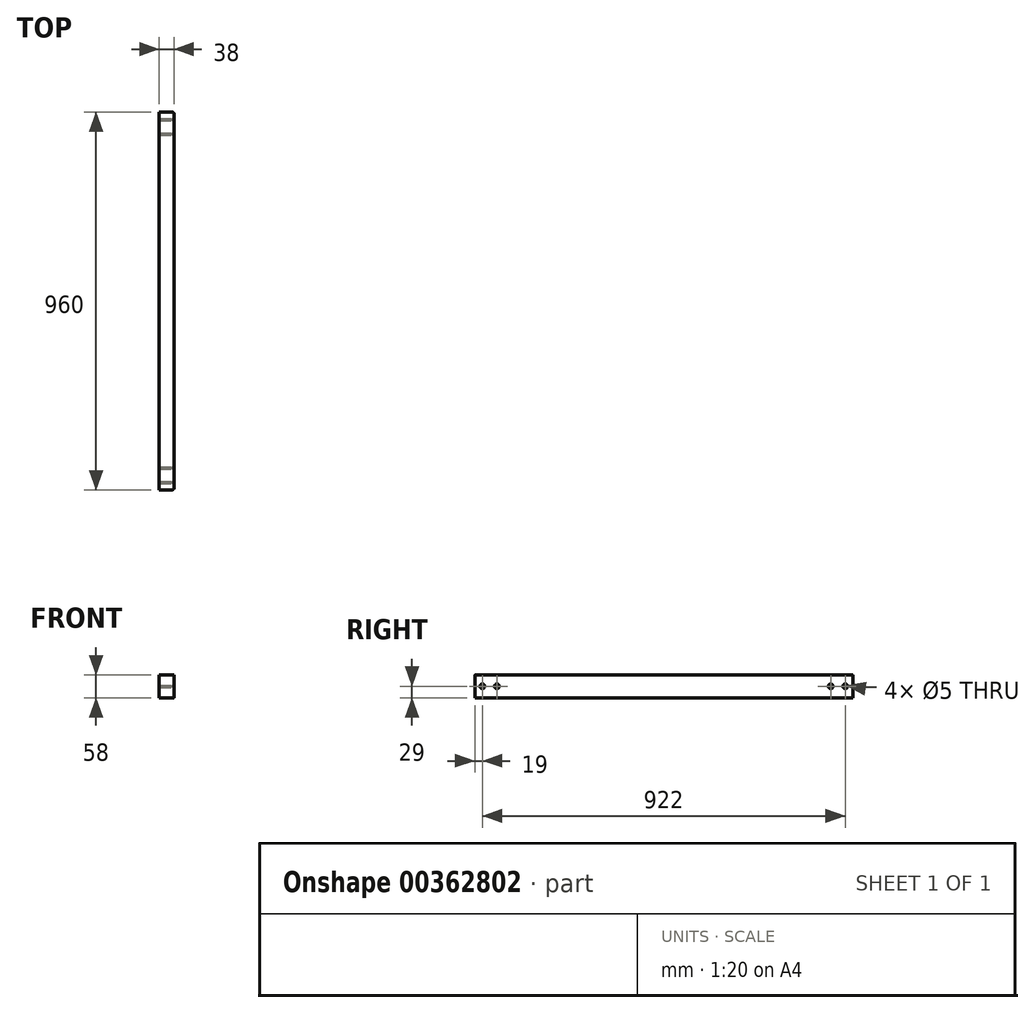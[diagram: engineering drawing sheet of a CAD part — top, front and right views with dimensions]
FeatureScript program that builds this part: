
annotation { "Feature Type Name" : "Feature", "Feature Type Description" : "" }
export const myFeature = defineFeature(function(context is Context, id is Id, definition is map)
    precondition{}
    {
        {
            var Q0;
            Q0=qCreatedBy(makeId("Front.planeOp"),FACE);
            var sketch = newSketch(context, id + "F0", { "sketchPlane" : qUnion([Q0])});
            skLineSegment(sketch, "E0.bottom", {"start": v(19, 29) * mm, "end": v(-19, 29) * mm});
            skLineSegment(sketch, "E0.top", {"start": v(19, -29) * mm, "end": v(-19, -29) * mm});
            skLineSegment(sketch, "E0.left", {"start": v(19, 29) * mm, "end": v(19, -29) * mm});
            skLineSegment(sketch, "E0.right", {"start": v(-19, 29) * mm, "end": v(-19, -29) * mm});
            skPoint(sketch, "E0.middle", {"position": v(0, 0) * mm});
            skSolve(sketch);
        }
        {
            var Q0;
            Q0=makeQuery(id+"F0.imprint","IMPRINT",FACE,{"disambiguationData":[TD([[makeQuery(id+"F0.imprint","IMPRINT",EDGE,{"derivedFrom":sQuery(id+"F0.wireOp",EDGE,"E0.bottom")}),1.0]])]});
            extrude(context, id + "F1", {"entities" : qUnion([Q0]), "oppositeDirection" : true, "depth" : 960 / 2 * mm});
        }
        {
            var Q0;
            Q0=makeQuery(id+"F1.opExtrude","SWEPT_FACE",FACE,{"disambiguationData":[OSD([sQuery(id+"F0.wireOp",EDGE,"E0.left")])]});
            var sketch = newSketch(context, id + "F2", { "sketchPlane" : qUnion([Q0])});
            skPoint(sketch, "E1", {"position": v(19, 0) * mm});
            skPoint(sketch, "E2", {"position": v(56, 0) * mm});
            skSolve(sketch);
        }
        {
            var Q0;
            Q0=makeQuery(id+"F1.opExtrude","CAP_EDGE",EDGE,{"disambiguationData":[OSD([sQuery(id+"F0.wireOp",EDGE,"E0.left")])],"isStart":true});
            fillet(context, id + "F3", {"entities" : qUnion([Q0]), "radius" : 5 * mm, "tangentPropagation" : true, "allowEdgeOverflow" : false});
        }
        {
            var Q0;
            Q0=sQuery(id+"F2.wireOp",VERTEX,"E1");
            var Q1;
            Q1=sQuery(id+"F2.wireOp",VERTEX,"E2");
            var Q2;
            Q2=makeQuery(id+"F1.opExtrude","SWEPT_BODY",BODY,{"disambiguationData":[OSD([sQuery(id+"F0.wireOp",EDGE,"E0.bottom"),sQuery(id+"F0.wireOp",EDGE,"E0.top"),sQuery(id+"F0.wireOp",EDGE,"E0.left"),sQuery(id+"F0.wireOp",EDGE,"E0.right")])]});
            hole(context, id + "F4", {"style" : HoleStyle.C_SINK, "endStyle" : HoleEndStyle.THROUGH, "holeDiameter" : 5 * mm, "cSinkDiameter" : 12 * mm, "cSinkAngle" : 90 * degree, "isTappedThrough" : true, "tappedDepth" : 12 * mm, "tapClearance" : 3, "locations" : qUnion([Q0, Q1]), "scope" : qUnion([Q2])});
        }
        {
            var Q0;
            Q0=makeQuery(id+"F1.opExtrude","SWEPT_BODY",BODY,{"disambiguationData":[OSD([sQuery(id+"F0.wireOp",EDGE,"E0.bottom"),sQuery(id+"F0.wireOp",EDGE,"E0.top"),sQuery(id+"F0.wireOp",EDGE,"E0.left"),sQuery(id+"F0.wireOp",EDGE,"E0.right")])]});
            var Q1;
            Q1=makeQuery(id+"F1.opExtrude","CAP_FACE",FACE,{"disambiguationData":[OSD([sQuery(id+"F0.wireOp",EDGE,"E0.bottom"),sQuery(id+"F0.wireOp",EDGE,"E0.top"),sQuery(id+"F0.wireOp",EDGE,"E0.left"),sQuery(id+"F0.wireOp",EDGE,"E0.right")])],"isStart":false});
            mirror(context, id + "F5", {"operationType" : NewBodyOperationType.ADD, "entities" : qUnion([Q0]), "mirrorPlane" : qUnion([Q1])});
        }
    });
